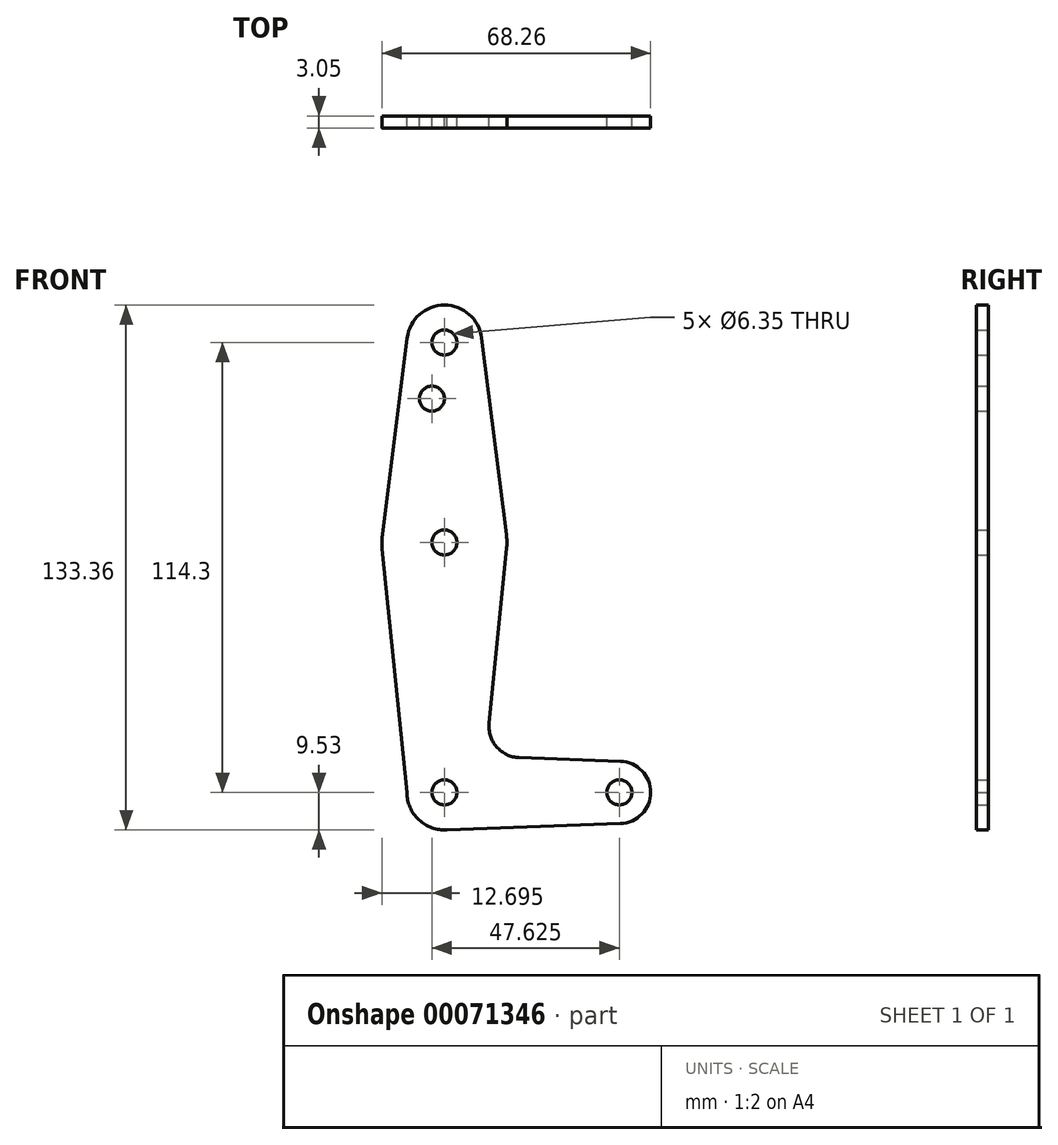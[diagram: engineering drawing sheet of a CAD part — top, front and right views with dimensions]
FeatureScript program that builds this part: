
annotation { "Feature Type Name" : "Feature", "Feature Type Description" : "" }
export const myFeature = defineFeature(function(context is Context, id is Id, definition is map)
    precondition{}
    {
        {
            var Q0;
            Q0=qCreatedBy(makeId("Front.planeOp"),FACE);
            var sketch = newSketch(context, id + "F0", { "sketchPlane" : qUnion([Q0])});
            skCircle(sketch, "E0", {"center": v(0, 0) * mm, "radius": 9.53 * mm});
            skCircle(sketch, "E1", {"center": v(0, 114.3) * mm, "radius": 9.53 * mm});
            skCircle(sketch, "E2", {"center": v(0, 63.5) * mm, "radius": 15.88 * mm});
            skCircle(sketch, "E3", {"center": v(44.45, 0) * mm, "radius": 7.94 * mm});
            skLineSegment(sketch, "E4", {"start": v(0, 114.3) * mm, "end": v(0, 63.5) * mm, "construction": true});
            skLineSegment(sketch, "E5", {"start": v(0, 63.5) * mm, "end": v(0, 0) * mm, "construction": true});
            skLineSegment(sketch, "E6", {"start": v(0, 0) * mm, "end": v(44.45, 0) * mm, "construction": true});
            skLineSegment(sketch, "E7", {"start": v(18.97, 8.85) * mm, "end": v(44.73, 7.93) * mm});
            skLineSegment(sketch, "E8", {"start": v(0, -9.53) * mm, "end": v(44.73, -7.93) * mm});
            skLineSegment(sketch, "E9", {"start": v(15.8, 61.91) * mm, "end": v(11.34, 17.59) * mm});
            skLineSegment(sketch, "E10", {"start": v(-9.53, 0) * mm, "end": v(-15.8, 61.9) * mm});
            skCircle(sketch, "E11", {"center": v(0, 114.3) * mm, "radius": 3.18 * mm});
            skCircle(sketch, "E12", {"center": v(0, 63.5) * mm, "radius": 3.18 * mm});
            skCircle(sketch, "E13", {"center": v(0, 0) * mm, "radius": 3.18 * mm});
            skCircle(sketch, "E14", {"center": v(44.45, 0) * mm, "radius": 3.18 * mm});
            skCircle(sketch, "E15", {"center": v(-3.17, 100.03) * mm, "radius": 3.18 * mm});
            skPoint(sketch, "E16.newPointB", {"position": v(0, 9.53) * mm});
            skArc(sketch, "E16.filletArc", {"start": v(11.34, 17.59) * mm, "mid": v(13.26, 11.57) * mm, "end": v(18.97, 8.85) * mm});
            skLineSegment(sketch, "E17", {"start": v(9.45, 115.5) * mm, "end": v(15.75, 65.48) * mm});
            skLineSegment(sketch, "E18.MirrorCS", {"start": v(-9.45, 115.5) * mm, "end": v(-15.75, 65.48) * mm});
            skSolve(sketch);
        }
        {
            var Q0;
            Q0 = qSketchRegion(id + "F0", true);
            extrude(context, id + "F1", {"entities" : qUnion([Q0]), "depth" : 3.05 * mm});
        }
    });
